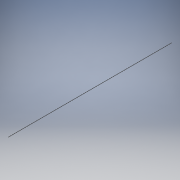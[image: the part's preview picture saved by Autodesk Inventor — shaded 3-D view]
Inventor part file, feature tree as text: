
AUTODESK INVENTOR PART (.ipt)
format: ipt  version: 2019 (Build 230136000, 136)  size: 144,384 bytes
history: native  units: in
note: dims shown in document units (in); Inventor stores cm internally (conversion verified against a paired STEP export)
features: extrude x1, sketch x1
ambient origin geometry x8: Origin, YZ Plane, XZ Plane, XY Plane, X Axis, Y Axis, Z Axis, Center Point
bodies: Solid1 (feature_tree)
feature tree (2):
  extrude  "Extrusion1"  [1 undecoded]
  sketch  "Sketch_1"  dims[d0=30.0in d1=0.0in]
note: 1 required parameter value undecoded (feature->parameter linkage not recoverable at this tier; creation-order binding heuristic only, values carry confidence <= 0.55)
